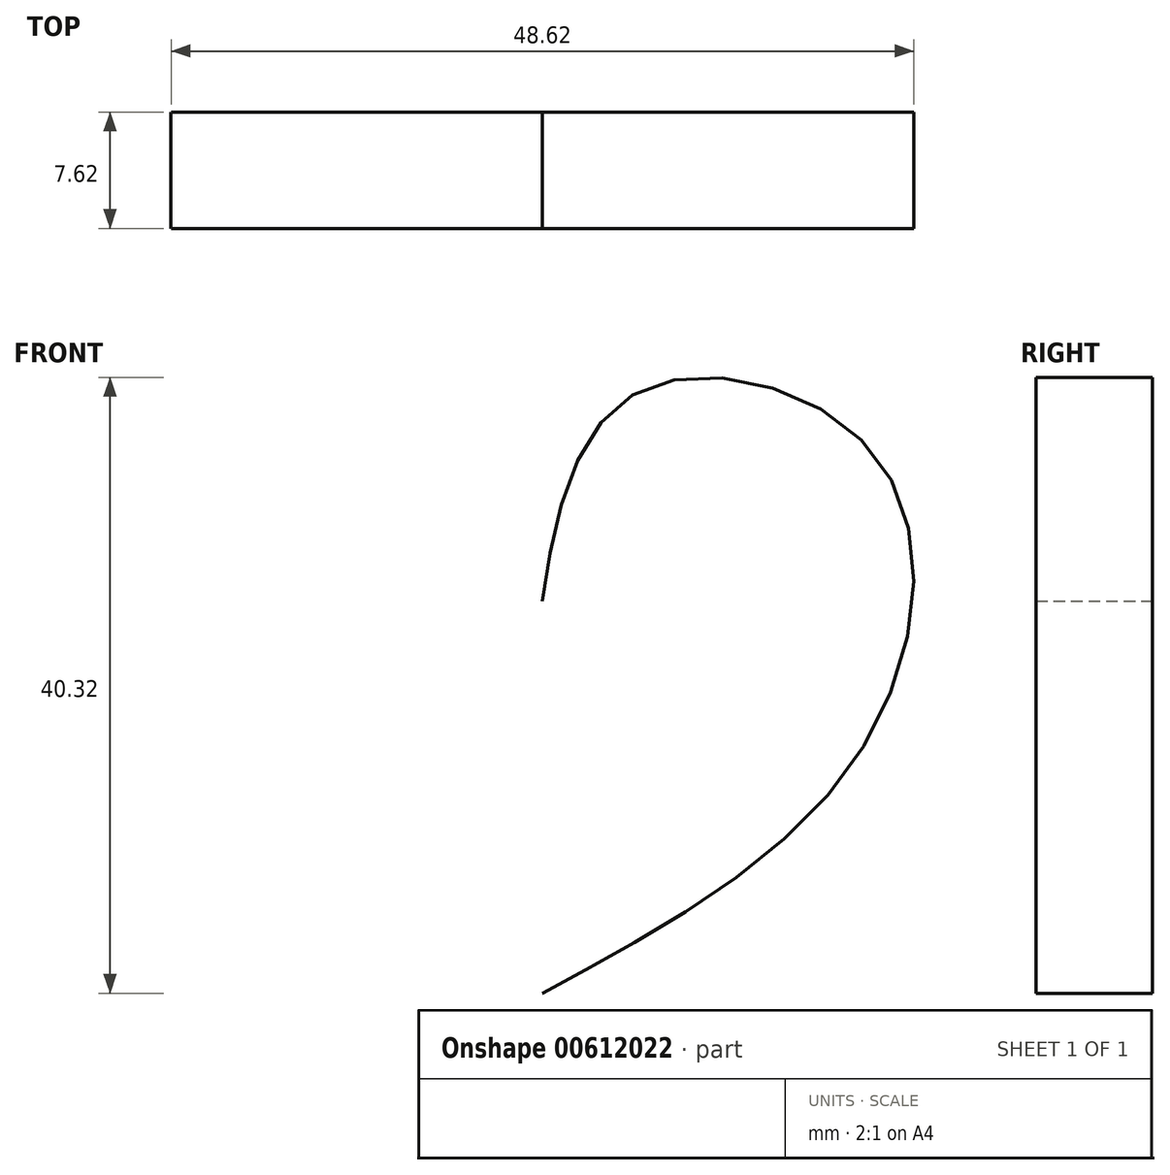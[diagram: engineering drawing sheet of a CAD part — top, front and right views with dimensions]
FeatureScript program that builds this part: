
annotation { "Feature Type Name" : "Feature", "Feature Type Description" : "" }
export const myFeature = defineFeature(function(context is Context, id is Id, definition is map)
    precondition{}
    {
        {
            var Q0;
            Q0=qCreatedBy(makeId("Front.planeOp"),FACE);
            var sketch = newSketch(context, id + "F0", { "sketchPlane" : qUnion([Q0])});
            skFitSpline(sketch, "E0", {"points": [v(0, 0) * mm, v(-6.19, 13.65) * mm, v(-21.85, 9.47) * mm, v(-20.2, -10.74) * mm, v(0, -25.67) * mm], "startDerivative": vector(-9.68, 71.3) * mm, "endDerivative": vector(61.02, -33.55) * mm});
            skFitSpline(sketch, "E1.MirrorCS", {"points": [v(0, 0) * mm, v(6.19, 13.65) * mm, v(21.85, 9.47) * mm, v(20.2, -10.74) * mm, v(0, -25.67) * mm], "startDerivative": vector(9.68, 71.3) * mm, "endDerivative": vector(-61.02, -33.55) * mm});
            skSolve(sketch);
        }
        {
            var Q0;
            Q0=makeQuery(id+"F0.imprint","IMPRINT",FACE,{"disambiguationData":[TD([[makeQuery(id+"F0.imprint","IMPRINT",EDGE,{"derivedFrom":sQuery(id+"F0.wireOp",EDGE,"E0")}),1.0]])]});
            extrude(context, id + "F1", {"entities" : qUnion([Q0]), "depth" : 7.62 * mm, "offsetDistance" : 25.4 * mm});
        }
    });
